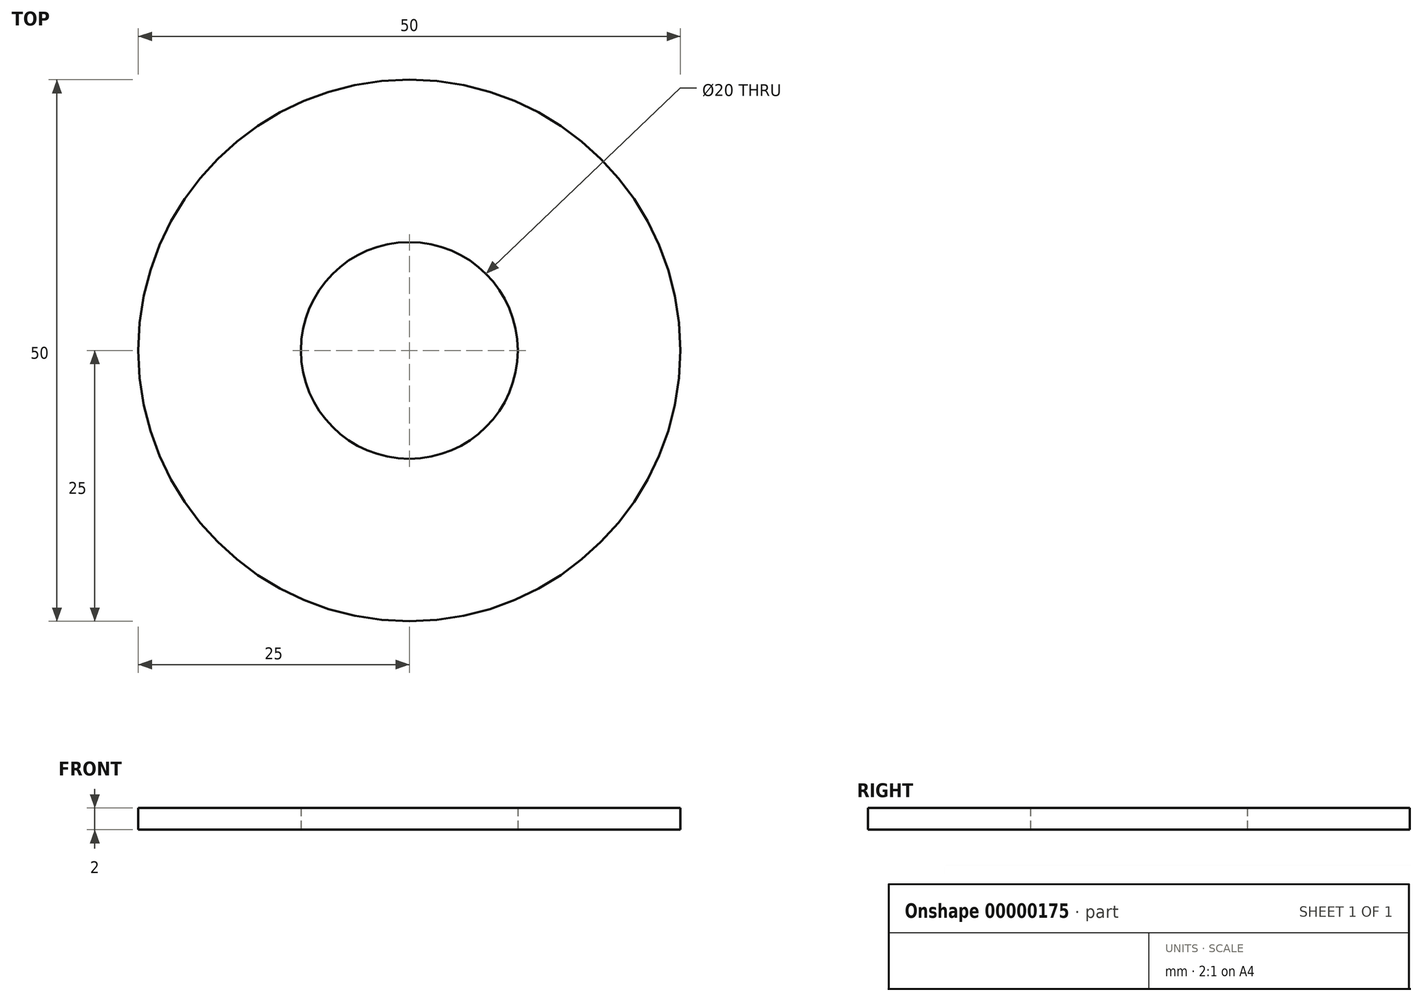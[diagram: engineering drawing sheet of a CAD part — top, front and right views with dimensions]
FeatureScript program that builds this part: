
annotation { "Feature Type Name" : "Feature", "Feature Type Description" : "" }
export const myFeature = defineFeature(function(context is Context, id is Id, definition is map)
    precondition{}
    {
        {
            var Q0;
            Q0=qCreatedBy(makeId("Top.planeOp"),FACE);
            var sketch = newSketch(context, id + "F0", { "sketchPlane" : qUnion([Q0])});
            skCircle(sketch, "E0", {"center": v(0, 0) * mm, "radius": 10 * mm});
            skCircle(sketch, "E1", {"center": v(0, 0) * mm, "radius": 25 * mm});
            skSolve(sketch);
        }
        {
            var Q0;
            Q0=makeQuery(id+"F0.imprint","IMPRINT",FACE,{"disambiguationData":[TD([[makeQuery(id+"F0.imprint","IMPRINT",EDGE,{"derivedFrom":sQuery(id+"F0.wireOp",EDGE,"E0")}),-1.0]])]});
            extrude(context, id + "F1", {"entities" : qUnion([Q0]), "depth" : 2 * mm});
        }
    });
